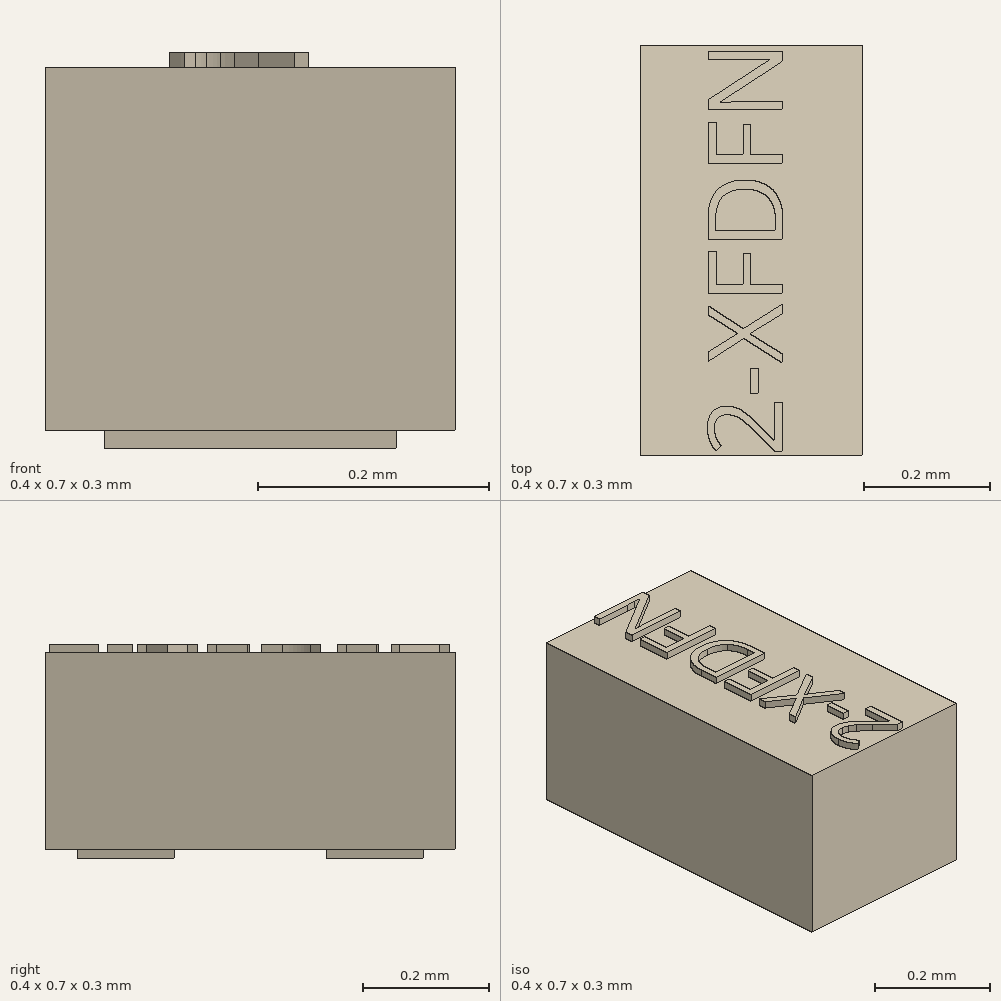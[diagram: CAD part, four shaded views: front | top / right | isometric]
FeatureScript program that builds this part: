
annotation { "Feature Type Name" : "Feature", "Feature Type Description" : "" }
export const myFeature = defineFeature(function(context is Context, id is Id, definition is map)
    precondition{}
    {
        {
            var Q0;
            Q0=qCreatedBy(makeId("Top.planeOp"),FACE);
            var sketch = newSketch(context, id + "F0", { "sketchPlane" : qUnion([Q0])});
            skLineSegment(sketch, "E0.bottom", {"start": v(-0.13, 0.12) * mm, "end": v(0.13, 0.12) * mm});
            skLineSegment(sketch, "E0.top", {"start": v(-0.13, 0.28) * mm, "end": v(0.13, 0.28) * mm});
            skLineSegment(sketch, "E0.left", {"start": v(-0.13, 0.12) * mm, "end": v(-0.13, 0.28) * mm});
            skLineSegment(sketch, "E0.right", {"start": v(0.13, 0.12) * mm, "end": v(0.13, 0.28) * mm});
            skLineSegment(sketch, "E1.bottom", {"start": v(-0.13, -0.28) * mm, "end": v(0.13, -0.28) * mm});
            skLineSegment(sketch, "E1.top", {"start": v(-0.13, -0.12) * mm, "end": v(0.13, -0.12) * mm});
            skLineSegment(sketch, "E1.left", {"start": v(-0.13, -0.28) * mm, "end": v(-0.13, -0.12) * mm});
            skLineSegment(sketch, "E1.right", {"start": v(0.13, -0.28) * mm, "end": v(0.13, -0.12) * mm});
            skSolve(sketch);
        }
        {
            var Q0;
            Q0 = qSketchRegion(id + "F0", true);
            extrude(context, id + "F1", {"entities" : qUnion([Q0]), "depth" : 0.02 * mm});
        }
        {
            var Q0;
            Q0=makeQuery(id+"F1.opExtrude","CAP_FACE",FACE,{"disambiguationData":[OSD([sQuery(id+"F0.wireOp",EDGE,"E0.bottom"),sQuery(id+"F0.wireOp",EDGE,"E0.top"),sQuery(id+"F0.wireOp",EDGE,"E0.left"),sQuery(id+"F0.wireOp",EDGE,"E0.right")])],"isStart":false});
            var sketch = newSketch(context, id + "F2", { "sketchPlane" : qUnion([Q0])});
            skLineSegment(sketch, "E2.bottom", {"start": v(-0.18, -0.33) * mm, "end": v(0.18, -0.33) * mm});
            skLineSegment(sketch, "E2.top", {"start": v(-0.18, 0.33) * mm, "end": v(0.18, 0.33) * mm});
            skLineSegment(sketch, "E2.left", {"start": v(-0.18, -0.33) * mm, "end": v(-0.18, 0.33) * mm});
            skLineSegment(sketch, "E2.right", {"start": v(0.18, -0.33) * mm, "end": v(0.18, 0.33) * mm});
            skSolve(sketch);
        }
        {
            var Q0;
            Q0 = qSketchRegion(id + "F2", true);
            extrude(context, id + "F3", {"entities" : qUnion([Q0]), "depth" : 0.31 * mm});
        }
        {
            var Q0;
            Q0=makeQuery(id+"F3.opExtrude","CAP_FACE",FACE,{"disambiguationData":[OSD([sQuery(id+"F2.wireOp",EDGE,"E2.bottom"),sQuery(id+"F2.wireOp",EDGE,"E2.top"),sQuery(id+"F2.wireOp",EDGE,"E2.left"),sQuery(id+"F2.wireOp",EDGE,"E2.right")])],"isStart":false});
            var sketch = newSketch(context, id + "F4", { "sketchPlane" : qUnion([Q0])});
            skText(sketch, "E3", { "text": "2-XFDFN", "fontName": "OpenSans-Regular.ttf"});
            const initialGuessF4  = {"E3": [5e-05, -0.00033, 0, 1, 0.00012]};
            skSetInitialGuess(sketch, initialGuessF4);
            skSolve(sketch);
        }
        {
            var Q0;
            Q0 = qSketchRegion(id + "F4", true);
            extrude(context, id + "F5", {"entities" : qUnion([Q0]), "operationType" : NewBodyOperationType.ADD, "depth" : 0.01 * mm});
        }
    });
